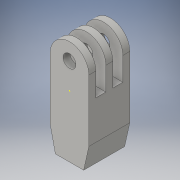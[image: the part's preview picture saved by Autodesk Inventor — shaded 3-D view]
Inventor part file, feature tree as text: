
AUTODESK INVENTOR PART (.ipt)
format: ipt  version: 2016 (Build 200138000, 138)  size: 167,936 bytes
history: native  units: in
note: dims shown in document units (in); Inventor stores cm internally (conversion verified against a paired STEP export)
features: sketch x5, extrude x4, fillet x1
ambient origin geometry x8: Origin, YZ Plane, XZ Plane, XY Plane, X Axis, Y Axis, Z Axis, Center Point
bodies: Solid1 (feature_tree)
feature tree (10):
  extrude  "Extrusion1"  Depth=0.2953in
  fillet  "Fillet1"  Radius=0.6496in
  extrude  "Extrusion8"  Depth=0.2559in
  extrude  "Extrusion9"  Depth=0.2953in
  sketch  "Sketch15"  dims[d47=0.1063in d48=0.1063in]
  extrude  "Extrusion10"  Depth=0.1063in
  sketch  "Sketch4"  dims[d0=0.2953in d1=0.2953in d2=0.6496in]
  sketch  "Sketch13"  dims[d3=0.1969in d4=0.2559in]
  sketch  "Sketch14"  dims[d5=0.626in d6=0.0in d7=0.2953in]
  sketch  "Sketch16"  dims[d49=0.1063in d50=0.626in d51=0.1535in d52=0.1535in d53=1.0in d54=0.0in d55=0.1575in d56=0.0in d57=0.5906in d58=0.7874in d59=0.3543in d60=0.0787in d61=0.0787in d62=0.3543in d63=0.626in d64=0.0in]
